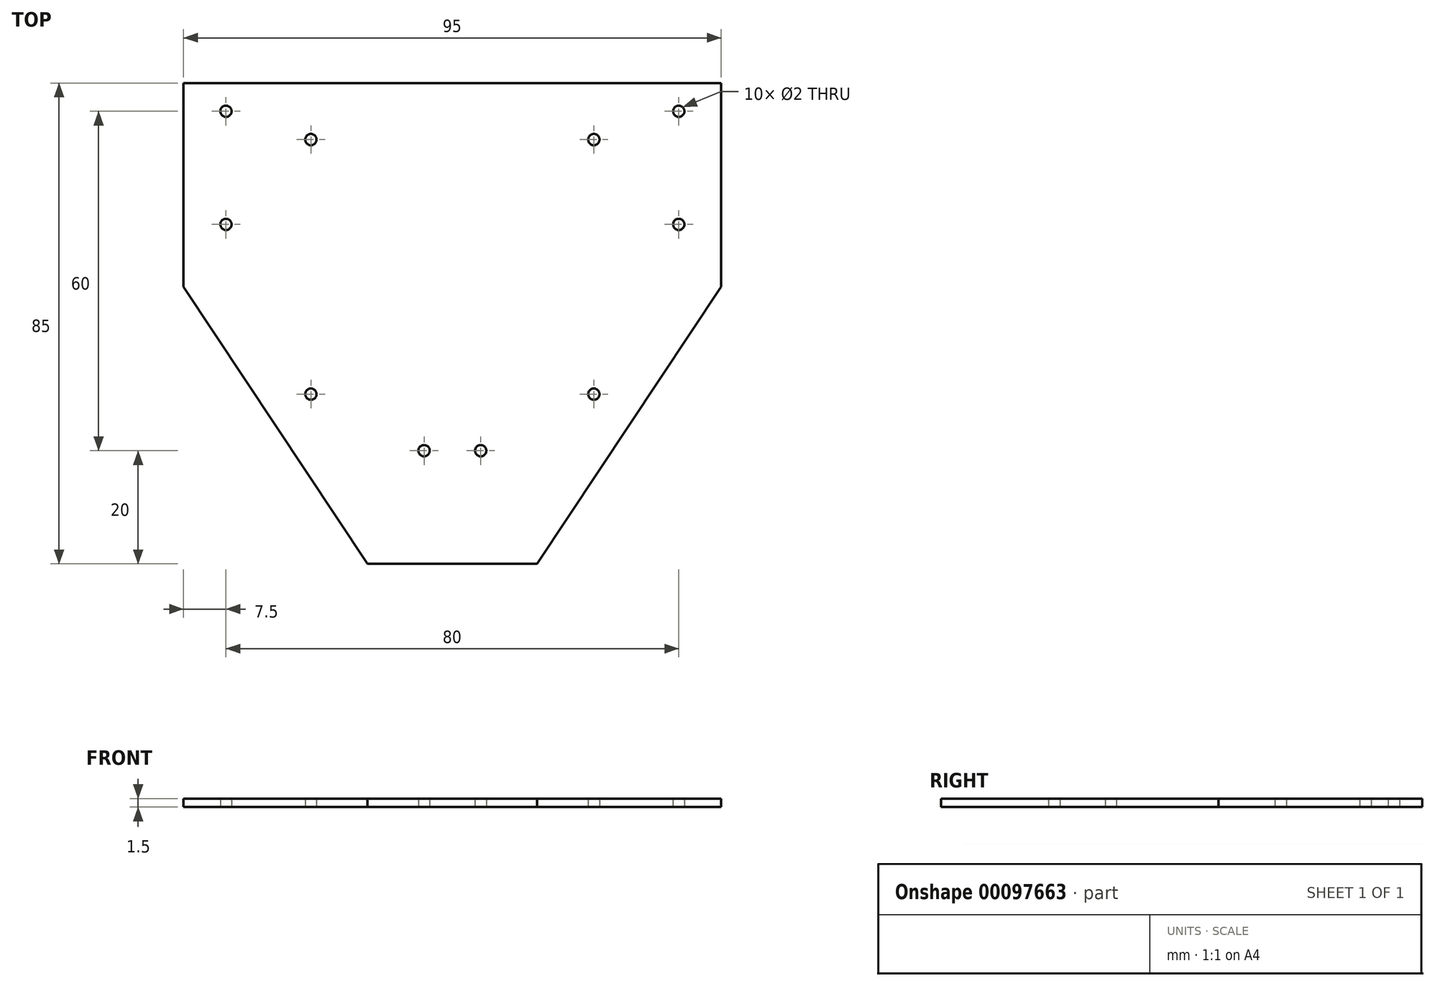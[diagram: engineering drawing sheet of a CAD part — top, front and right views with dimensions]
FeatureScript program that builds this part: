
annotation { "Feature Type Name" : "Feature", "Feature Type Description" : "" }
export const myFeature = defineFeature(function(context is Context, id is Id, definition is map)
    precondition{}
    {
        {
            var Q0;
            Q0=qCreatedBy(makeId("Top.planeOp"),FACE);
            var sketch = newSketch(context, id + "F0", { "sketchPlane" : qUnion([Q0])});
            skLineSegment(sketch, "E0.bottom", {"start": v(47.5, -42.5) * mm, "end": v(-47.5, -42.5) * mm});
            skLineSegment(sketch, "E0.top", {"start": v(47.5, 42.5) * mm, "end": v(-47.5, 42.5) * mm});
            skLineSegment(sketch, "E0.left", {"start": v(47.5, -42.5) * mm, "end": v(47.5, 42.5) * mm});
            skLineSegment(sketch, "E0.right", {"start": v(-47.5, -42.5) * mm, "end": v(-47.5, 42.5) * mm});
            skPoint(sketch, "E0.middle", {"position": v(0, 0) * mm});
            skCircle(sketch, "E1", {"center": v(-5, -22.5) * mm, "radius": 1 * mm});
            skCircle(sketch, "E2", {"center": v(40, 37.5) * mm, "radius": 1 * mm});
            skCircle(sketch, "E3", {"center": v(40, 17.5) * mm, "radius": 1 * mm});
            skCircle(sketch, "E4.MirrorC", {"center": v(-40, 37.5) * mm, "radius": 1 * mm});
            skCircle(sketch, "E5.MirrorC", {"center": v(-40, 17.5) * mm, "radius": 1 * mm});
            skCircle(sketch, "E6.MirrorC", {"center": v(5, -22.5) * mm, "radius": 1 * mm});
            skLineSegment(sketch, "E7", {"start": v(-47.5, 0) * mm, "end": v(47.5, 0) * mm, "construction": true});
            skCircle(sketch, "E8", {"center": v(25, 32.5) * mm, "radius": 1 * mm});
            skCircle(sketch, "E9", {"center": v(25, -12.5) * mm, "radius": 1 * mm});
            skCircle(sketch, "E10.MirrorC", {"center": v(-25, 32.5) * mm, "radius": 1 * mm});
            skCircle(sketch, "E11.MirrorC", {"center": v(-25, -12.5) * mm, "radius": 1 * mm});
            skSolve(sketch);
        }
        {
            var Q0;
            Q0 = qSketchRegion(id + "F0", true);
            extrude(context, id + "F1", {"entities" : qUnion([Q0]), "depth" : 1.5 * mm});
        }
        {
            var Q0;
            Q0=makeQuery(id+"F1.opExtrude","CAP_FACE",FACE,{"disambiguationData":[OSD([sQuery(id+"F0.wireOp",EDGE,"E0.bottom"),sQuery(id+"F0.wireOp",EDGE,"E0.top"),sQuery(id+"F0.wireOp",EDGE,"E0.left"),sQuery(id+"F0.wireOp",EDGE,"E0.right"),sQuery(id+"F0.wireOp",EDGE,"E1"),sQuery(id+"F0.wireOp",EDGE,"E2"),sQuery(id+"F0.wireOp",EDGE,"E3"),sQuery(id+"F0.wireOp",EDGE,"E4.MirrorC"),sQuery(id+"F0.wireOp",EDGE,"E5.MirrorC"),sQuery(id+"F0.wireOp",EDGE,"E6.MirrorC")])],"isStart":false});
            var sketch = newSketch(context, id + "F2", { "sketchPlane" : qUnion([Q0])});
            skLineSegment(sketch, "E12", {"start": v(-47.5, 6.5) * mm, "end": v(-15, -42.5) * mm});
            skPoint(sketch, "E13", {"position": v(-40, 17.5) * mm});
            skLineSegment(sketch, "E14.MirrorCS", {"start": v(47.5, 6.5) * mm, "end": v(15, -42.5) * mm});
            skLineSegment(sketch, "E15", {"start": v(-47.5, 6.5) * mm, "end": v(-47.5, -42.5) * mm});
            skLineSegment(sketch, "E16", {"start": v(-47.5, -42.5) * mm, "end": v(-15, -42.5) * mm});
            skLineSegment(sketch, "E17.MirrorCS", {"start": v(47.5, 6.5) * mm, "end": v(47.5, -42.5) * mm});
            skLineSegment(sketch, "E18.MirrorCS", {"start": v(47.5, -42.5) * mm, "end": v(15, -42.5) * mm});
            skSolve(sketch);
        }
        {
            var Q0;
            Q0 = qSketchRegion(id + "F2", true);
            extrude(context, id + "F3", {"entities" : qUnion([Q0]), "operationType" : NewBodyOperationType.REMOVE, "endBound" : BoundingType.UP_TO_NEXT, "oppositeDirection" : true, "depth" : 25 * mm});
        }
    });
